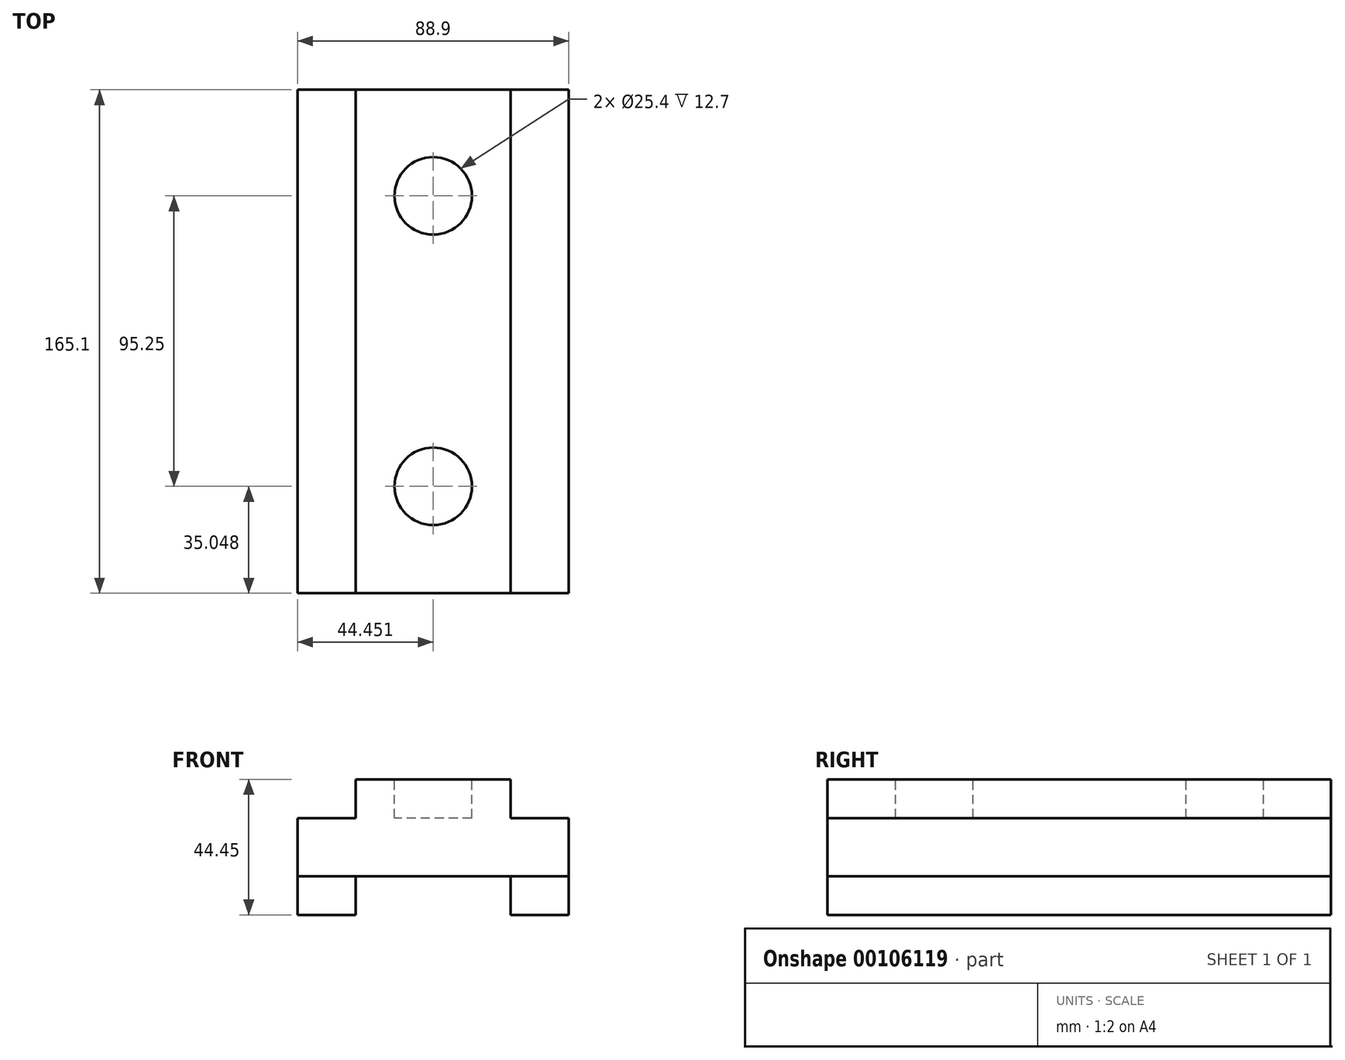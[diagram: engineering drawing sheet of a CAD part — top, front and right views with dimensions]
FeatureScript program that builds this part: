
annotation { "Feature Type Name" : "Feature", "Feature Type Description" : "" }
export const myFeature = defineFeature(function(context is Context, id is Id, definition is map)
    precondition{}
    {
        {
            var Q0;
            Q0=qCreatedBy(makeId("Top.planeOp"),FACE);
            var sketch = newSketch(context, id + "F0", { "sketchPlane" : qUnion([Q0])});
            skLineSegment(sketch, "E0.bottom", {"start": v(-58.37, 99.98) * mm, "end": v(-39.32, 99.98) * mm});
            skLineSegment(sketch, "E0.top", {"start": v(-58.37, -65.12) * mm, "end": v(-39.32, -65.12) * mm});
            skLineSegment(sketch, "E0.left", {"start": v(-58.37, 99.98) * mm, "end": v(-58.37, -65.12) * mm});
            skLineSegment(sketch, "E0.right", {"start": v(-39.32, 99.98) * mm, "end": v(-39.32, -65.12) * mm});
            skLineSegment(sketch, "E1", {"start": v(-39.32, -65.12) * mm, "end": v(11.48, -65.12) * mm});
            skLineSegment(sketch, "E2.bottom", {"start": v(11.48, -65.12) * mm, "end": v(30.53, -65.12) * mm});
            skLineSegment(sketch, "E2.top", {"start": v(11.48, 99.98) * mm, "end": v(30.53, 99.98) * mm});
            skLineSegment(sketch, "E2.left", {"start": v(11.48, -65.12) * mm, "end": v(11.48, 99.98) * mm});
            skLineSegment(sketch, "E2.right", {"start": v(30.53, -65.12) * mm, "end": v(30.53, 99.98) * mm});
            skSolve(sketch);
        }
        {
            var Q0;
            Q0=makeQuery(id+"F0.imprint","IMPRINT",FACE,{"disambiguationData":[TD([[makeQuery(id+"F0.imprint","IMPRINT",EDGE,{"derivedFrom":sQuery(id+"F0.wireOp",EDGE,"E0.bottom")}),-1.0]])]});
            var Q1;
            Q1=makeQuery(id+"F0.imprint","IMPRINT",FACE,{"disambiguationData":[TD([[makeQuery(id+"F0.imprint","IMPRINT",EDGE,{"derivedFrom":sQuery(id+"F0.wireOp",EDGE,"E2.bottom")}),1.0]])]});
            extrude(context, id + "F1", {"entities" : qUnion([Q0, Q1]), "depth" : 12.7 * mm});
        }
        {
            var Q0;
            Q0=makeQuery(id+"F1.opExtrude","CAP_FACE",FACE,{"disambiguationData":[OSD([sQuery(id+"F0.wireOp",EDGE,"E2.bottom"),sQuery(id+"F0.wireOp",EDGE,"E2.top"),sQuery(id+"F0.wireOp",EDGE,"E2.left"),sQuery(id+"F0.wireOp",EDGE,"E2.right")])],"isStart":false});
            var sketch = newSketch(context, id + "F2", { "sketchPlane" : qUnion([Q0])});
            skLineSegment(sketch, "E3.bottom", {"start": v(30.53, 99.98) * mm, "end": v(-58.37, 99.98) * mm});
            skLineSegment(sketch, "E3.top", {"start": v(30.53, -65.12) * mm, "end": v(-58.37, -65.12) * mm});
            skLineSegment(sketch, "E3.left", {"start": v(30.53, 99.98) * mm, "end": v(30.53, -65.12) * mm});
            skLineSegment(sketch, "E3.right", {"start": v(-58.37, 99.98) * mm, "end": v(-58.37, -65.12) * mm});
            skSolve(sketch);
        }
        {
            var Q0;
            {var subQ2=sQuery(id+"F2.wireOp",EDGE,"E3.right");Q0=makeQuery(id+"F2.imprint","IMPRINT",FACE,{"disambiguationData":[TD([[makeQuery(id+"F2.imprint","IMPRINT",EDGE,{"derivedFrom":subQ2}),1.0]])]});}
            var Q1;
            {var subQ2=sQuery(id+"F2.wireOp",EDGE,"E3.left");Q1=makeQuery(id+"F2.imprint","IMPRINT",FACE,{"disambiguationData":[TD([[makeQuery(id+"F2.imprint","IMPRINT",EDGE,{"derivedFrom":subQ2}),1.0]])]});}
            extrude(context, id + "F3", {"entities" : qUnion([Q0, Q1]), "depth" : 19.05 * mm});
        }
        {
            var Q0;
            Q0=makeQuery(id+"F3.opExtrude","CAP_FACE",FACE,{"disambiguationData":[OSD([sQuery(id+"F2.wireOp",EDGE,"E3.bottom"),sQuery(id+"F2.wireOp",EDGE,"E3.top"),sQuery(id+"F2.wireOp",EDGE,"E3.left"),sQuery(id+"F2.wireOp",EDGE,"E3.right")])],"isStart":false});
            var sketch = newSketch(context, id + "F4", { "sketchPlane" : qUnion([Q0])});
            skLineSegment(sketch, "E4", {"start": v(-58.37, -65.12) * mm, "end": v(-39.32, -65.12) * mm});
            skLineSegment(sketch, "E5.bottom", {"start": v(-39.32, -65.12) * mm, "end": v(11.48, -65.12) * mm});
            skLineSegment(sketch, "E5.top", {"start": v(-39.32, 99.98) * mm, "end": v(11.48, 99.98) * mm});
            skLineSegment(sketch, "E5.left", {"start": v(-39.32, -65.12) * mm, "end": v(-39.32, 99.98) * mm});
            skLineSegment(sketch, "E5.right", {"start": v(11.48, -65.12) * mm, "end": v(11.48, 99.98) * mm});
            skSolve(sketch);
        }
        {
            var Q0;
            Q0 = qSketchRegion(id + "F4", true);
            extrude(context, id + "F5", {"entities" : qUnion([Q0]), "operationType" : NewBodyOperationType.ADD, "depth" : 12.7 * mm});
        }
        {
            var Q0;
            Q0=makeQuery(id+"F5.opExtrude","CAP_FACE",FACE,{"disambiguationData":[OSD([sQuery(id+"F4.wireOp",EDGE,"E5.bottom"),sQuery(id+"F4.wireOp",EDGE,"E5.top"),sQuery(id+"F4.wireOp",EDGE,"E5.left"),sQuery(id+"F4.wireOp",EDGE,"E5.right")])],"isStart":false});
            var sketch = newSketch(context, id + "F6", { "sketchPlane" : qUnion([Q0])});
            skLineSegment(sketch, "E6", {"start": v(-39.32, -65.12) * mm, "end": v(-13.92, -65.12) * mm});
            skLineSegment(sketch, "E7", {"start": v(-13.92, -65.12) * mm, "end": v(-13.92, -30.07) * mm});
            skCircle(sketch, "E8", {"center": v(-13.92, -30.07) * mm, "radius": 12.7 * mm});
            skLineSegment(sketch, "E9", {"start": v(-13.92, -30.07) * mm, "end": v(-13.92, 65.18) * mm});
            skCircle(sketch, "E10", {"center": v(-13.92, 65.18) * mm, "radius": 12.7 * mm});
            skSolve(sketch);
        }
        {
            var Q0;
            {var subQ0=sQuery(id+"F6.wireOp",EDGE,"E9");var subQ1=sQuery(id+"F6.wireOp",EDGE,"E7");var subQ2=makeQuery(id+"F6.imprint","INTERSECT",VERTEX,{"derivedFrom":[subQ1,subQ0]});Q0=makeQuery(id+"F6.imprint","IMPRINT",FACE,{"disambiguationData":[TD([[makeQuery(id+"F6.imprint","IMPRINT",EDGE,{"disambiguationData":[TD([[subQ2,1.0]])],"derivedFrom":subQ1}),-1.0]])]});}
            var Q1;
            {var subQ0=sQuery(id+"F6.wireOp",EDGE,"E9");var subQ1=sQuery(id+"F6.wireOp",EDGE,"E7");var subQ2=makeQuery(id+"F6.imprint","INTERSECT",VERTEX,{"derivedFrom":[subQ1,subQ0]});Q1=makeQuery(id+"F6.imprint","IMPRINT",FACE,{"disambiguationData":[TD([[makeQuery(id+"F6.imprint","IMPRINT",EDGE,{"disambiguationData":[TD([[subQ2,1.0]])],"derivedFrom":subQ1}),1.0]])]});}
            var Q2;
            Q2=makeQuery(id+"F6.imprint","IMPRINT",FACE,{"disambiguationData":[TD([[makeQuery(id+"F6.imprint","IMPRINT",EDGE,{"derivedFrom":sQuery(id+"F6.wireOp",EDGE,"E10")}),1.0]])]});
            extrude(context, id + "F7", {"entities" : qUnion([Q0, Q1, Q2]), "operationType" : NewBodyOperationType.REMOVE, "oppositeDirection" : true, "depth" : 12.7 * mm});
        }
    });
